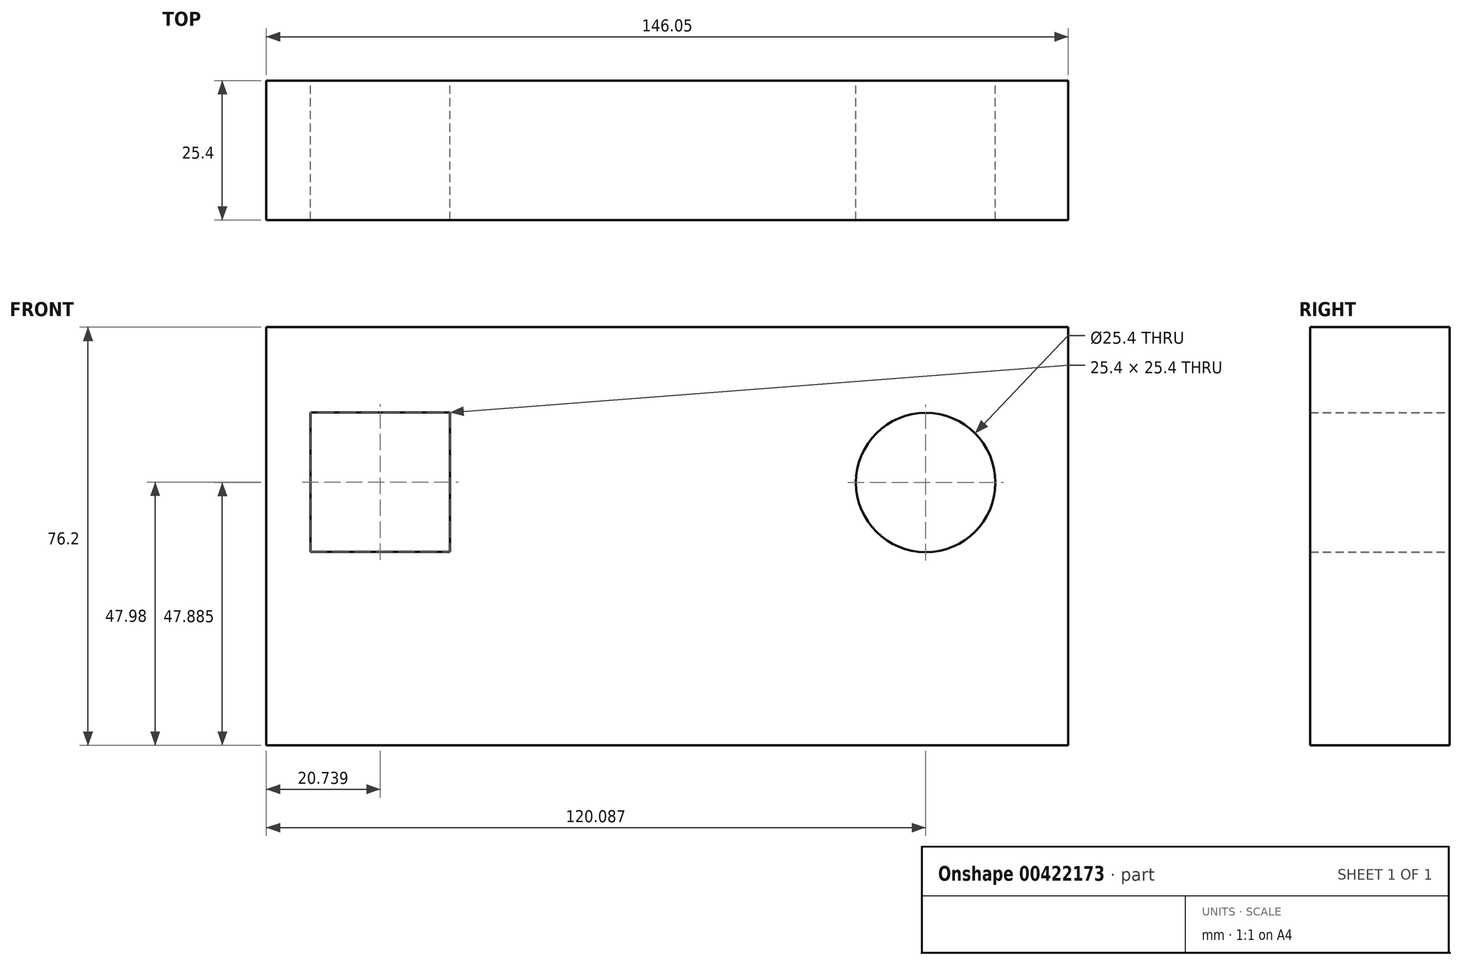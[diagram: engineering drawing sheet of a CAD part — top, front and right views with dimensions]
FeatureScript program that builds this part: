
annotation { "Feature Type Name" : "Feature", "Feature Type Description" : "" }
export const myFeature = defineFeature(function(context is Context, id is Id, definition is map)
    precondition{}
    {
        {
            var Q0;
            Q0=qCreatedBy(makeId("Front.planeOp"),FACE);
            var sketch = newSketch(context, id + "F0", { "sketchPlane" : qUnion([Q0])});
            skPoint(sketch, "E0.end.orphan", {"position": v(-59.3, -3.85) * mm});
            skPoint(sketch, "E1.end.orphan", {"position": v(-76.06, 16.67) * mm});
            skPoint(sketch, "E1.start.orphan", {"position": v(-76.06, 92.87) * mm});
            skLineSegment(sketch, "E2.bottom", {"start": v(-70.7, 40.92) * mm, "end": v(75.35, 40.92) * mm});
            skLineSegment(sketch, "E2.top", {"start": v(-70.7, -35.28) * mm, "end": v(75.35, -35.28) * mm});
            skLineSegment(sketch, "E2.left", {"start": v(-70.7, 40.92) * mm, "end": v(-70.7, -35.28) * mm});
            skLineSegment(sketch, "E2.right", {"start": v(75.35, 40.92) * mm, "end": v(75.35, -35.28) * mm});
            skLineSegment(sketch, "E3.bottom", {"start": v(-62.66, 25.4) * mm, "end": v(-37.26, 25.4) * mm});
            skLineSegment(sketch, "E3.top", {"start": v(-62.66, 0) * mm, "end": v(-37.26, 0) * mm});
            skLineSegment(sketch, "E3.left", {"start": v(-62.66, 25.4) * mm, "end": v(-62.66, 0) * mm});
            skLineSegment(sketch, "E3.right", {"start": v(-37.26, 25.4) * mm, "end": v(-37.26, 0) * mm});
            skCircle(sketch, "E4", {"center": v(49.39, 12.6) * mm, "radius": 12.7 * mm});
            skSolve(sketch);
        }
        {
            var Q0;
            Q0=makeQuery(id+"F0.imprint","IMPRINT",FACE,{"disambiguationData":[TD([[makeQuery(id+"F0.imprint","IMPRINT",EDGE,{"derivedFrom":sQuery(id+"F0.wireOp",EDGE,"E2.bottom")}),-1.0]])]});
            extrude(context, id + "F1", {"entities" : qUnion([Q0]), "depth" : 25.4 * mm});
        }
    });
